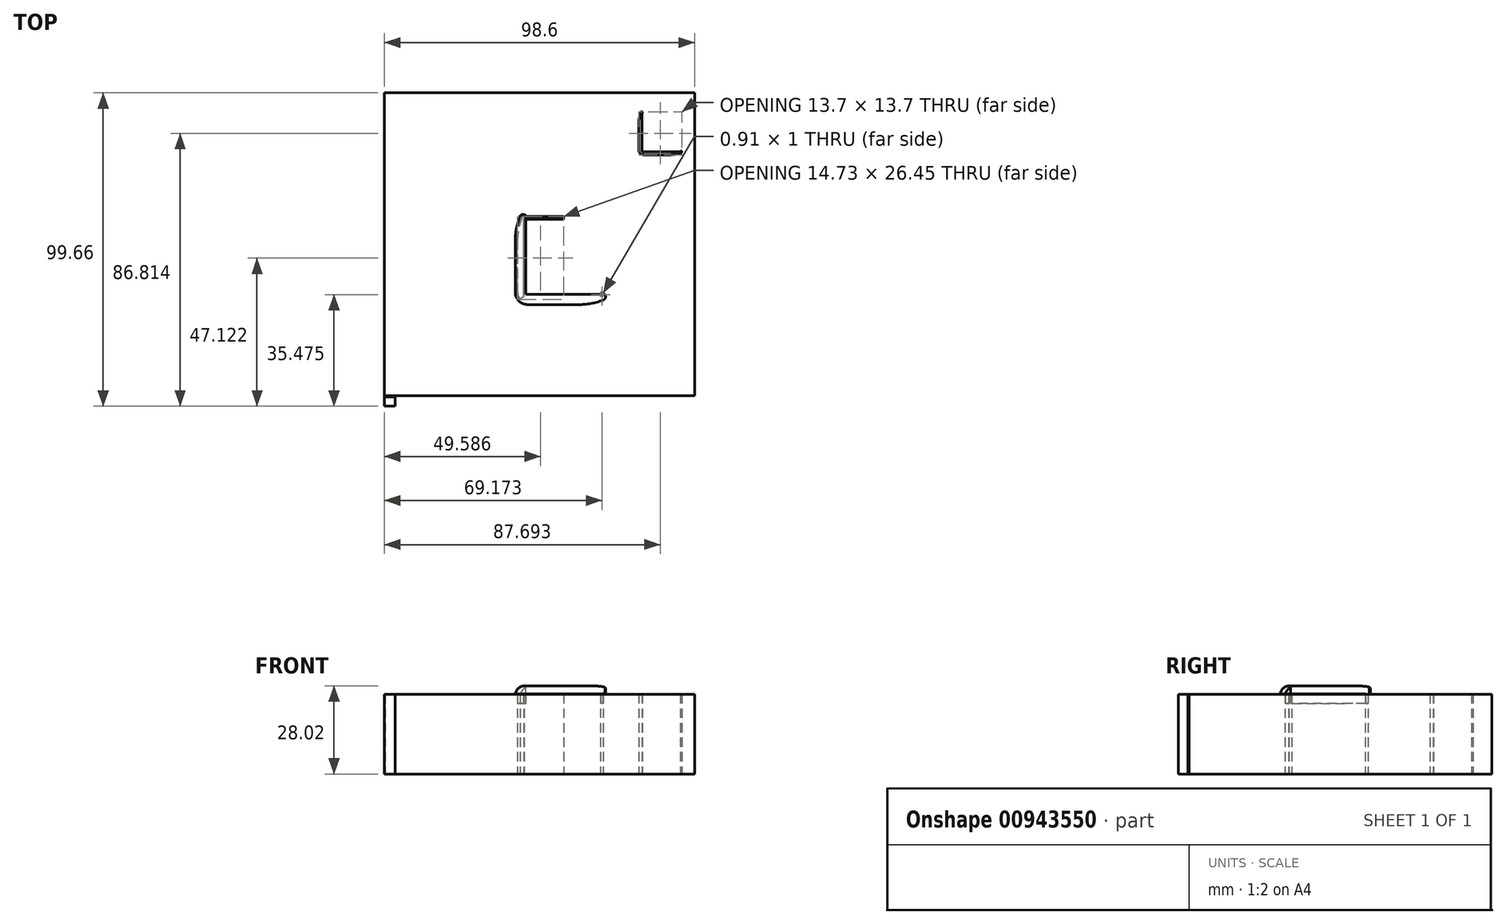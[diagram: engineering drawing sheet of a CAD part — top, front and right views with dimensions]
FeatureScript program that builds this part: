
annotation { "Feature Type Name" : "Feature", "Feature Type Description" : "" }
export const myFeature = defineFeature(function(context is Context, id is Id, definition is map)
    precondition{}
    {
        {
            var Q0;
            Q0=qCreatedBy(makeId("Top.planeOp"),FACE);
            var sketch = newSketch(context, id + "F0", { "sketchPlane" : qUnion([Q0])});
            skLineSegment(sketch, "E0", {"start": v(-49.3, -64.38) * mm, "end": v(49.3, -64.38) * mm});
            skLineSegment(sketch, "E1", {"start": v(49.3, -64.38) * mm, "end": v(49.3, 64.38) * mm});
            skLineSegment(sketch, "E2", {"start": v(49.3, 64.38) * mm, "end": v(-49.3, 64.38) * mm});
            skLineSegment(sketch, "E3", {"start": v(-49.3, 64.38) * mm, "end": v(-49.3, -64.38) * mm});
            skLineSegment(sketch, "E4", {"start": v(-49.3, 60.15) * mm, "end": v(49.3, 60.15) * mm});
            skLineSegment(sketch, "E5", {"start": v(49.3, 60.15) * mm, "end": v(49.3, 59.97) * mm});
            skLineSegment(sketch, "E6", {"start": v(49.3, 59.97) * mm, "end": v(-49.3, 59.97) * mm});
            skLineSegment(sketch, "E7", {"start": v(-49.3, 59.97) * mm, "end": v(-49.3, 60.15) * mm});
            skLineSegment(sketch, "E8", {"start": v(15.26, 64.38) * mm, "end": v(15.43, 64.38) * mm});
            skLineSegment(sketch, "E9", {"start": v(15.43, 64.38) * mm, "end": v(15.43, 59.97) * mm});
            skLineSegment(sketch, "E10", {"start": v(15.43, 59.97) * mm, "end": v(15.26, 59.97) * mm});
            skLineSegment(sketch, "E11", {"start": v(15.26, 59.97) * mm, "end": v(15.26, 64.38) * mm});
            skLineSegment(sketch, "E12", {"start": v(-49.12, -36.34) * mm, "end": v(49.3, -36.34) * mm});
            skLineSegment(sketch, "E13", {"start": v(49.3, -36.34) * mm, "end": v(49.3, -36.69) * mm});
            skLineSegment(sketch, "E14", {"start": v(49.3, -36.69) * mm, "end": v(-49.12, -36.69) * mm});
            skLineSegment(sketch, "E15", {"start": v(-49.12, -36.69) * mm, "end": v(-49.12, -36.34) * mm});
            skLineSegment(sketch, "E16", {"start": v(-6.44, -36.51) * mm, "end": v(-6.09, -36.51) * mm});
            skLineSegment(sketch, "E17", {"start": v(-6.09, -36.51) * mm, "end": v(-6.09, -64.2) * mm});
            skLineSegment(sketch, "E18", {"start": v(-6.09, -64.2) * mm, "end": v(-6.44, -64.2) * mm});
            skLineSegment(sketch, "E19", {"start": v(-6.44, -64.2) * mm, "end": v(-6.44, -36.51) * mm});
            skLineSegment(sketch, "E20", {"start": v(-6.44, -45.33) * mm, "end": v(49.12, -45.33) * mm});
            skLineSegment(sketch, "E21", {"start": v(49.12, -45.33) * mm, "end": v(49.12, -45.68) * mm});
            skLineSegment(sketch, "E22", {"start": v(49.12, -45.68) * mm, "end": v(-6.44, -45.68) * mm});
            skLineSegment(sketch, "E23", {"start": v(-6.44, -45.68) * mm, "end": v(-6.44, -45.33) * mm});
            skLineSegment(sketch, "E24", {"start": v(-6.44, -49.04) * mm, "end": v(49.12, -49.04) * mm});
            skLineSegment(sketch, "E25", {"start": v(49.12, -49.04) * mm, "end": v(49.12, -49.39) * mm});
            skLineSegment(sketch, "E26", {"start": v(49.12, -49.39) * mm, "end": v(-6.44, -49.39) * mm});
            skLineSegment(sketch, "E27", {"start": v(-6.44, -49.39) * mm, "end": v(-6.44, -49.04) * mm});
            skLineSegment(sketch, "E28", {"start": v(-6.09, -52.92) * mm, "end": v(49.3, -52.92) * mm});
            skLineSegment(sketch, "E29", {"start": v(49.3, -52.92) * mm, "end": v(49.3, -53.1) * mm});
            skLineSegment(sketch, "E30", {"start": v(49.3, -53.1) * mm, "end": v(-6.09, -53.1) * mm});
            skLineSegment(sketch, "E31", {"start": v(-6.09, -53.1) * mm, "end": v(-6.09, -52.92) * mm});
            skLineSegment(sketch, "E32", {"start": v(-6.09, -56.62) * mm, "end": v(49.3, -56.62) * mm});
            skLineSegment(sketch, "E33", {"start": v(49.3, -56.62) * mm, "end": v(49.3, -56.8) * mm});
            skLineSegment(sketch, "E34", {"start": v(49.3, -56.8) * mm, "end": v(-6.09, -56.8) * mm});
            skLineSegment(sketch, "E35", {"start": v(-6.09, -56.8) * mm, "end": v(-6.09, -56.62) * mm});
            skLineSegment(sketch, "E36", {"start": v(-6.09, -60.32) * mm, "end": v(49.3, -60.32) * mm});
            skLineSegment(sketch, "E37", {"start": v(49.3, -60.32) * mm, "end": v(49.3, -60.5) * mm});
            skLineSegment(sketch, "E38", {"start": v(49.3, -60.5) * mm, "end": v(-6.09, -60.5) * mm});
            skLineSegment(sketch, "E39", {"start": v(-6.09, -60.5) * mm, "end": v(-6.09, -60.32) * mm});
            skLineSegment(sketch, "E40", {"start": v(21.25, -49.04) * mm, "end": v(21.6, -49.04) * mm});
            skLineSegment(sketch, "E41", {"start": v(21.6, -49.04) * mm, "end": v(21.6, -64.2) * mm});
            skLineSegment(sketch, "E42", {"start": v(21.6, -64.2) * mm, "end": v(21.25, -64.2) * mm});
            skLineSegment(sketch, "E43", {"start": v(21.25, -64.2) * mm, "end": v(21.25, -49.04) * mm});
            skLineSegment(sketch, "E44", {"start": v(-49.3, -47.8) * mm, "end": v(-6.09, -47.8) * mm});
            skLineSegment(sketch, "E45", {"start": v(-6.09, -47.8) * mm, "end": v(-6.09, -48.15) * mm});
            skLineSegment(sketch, "E46", {"start": v(-6.09, -48.15) * mm, "end": v(-49.3, -48.15) * mm});
            skLineSegment(sketch, "E47", {"start": v(-49.3, -48.15) * mm, "end": v(-49.3, -47.8) * mm});
            skLineSegment(sketch, "E48", {"start": v(-49.3, -53.8) * mm, "end": v(-6.09, -53.8) * mm});
            skLineSegment(sketch, "E49", {"start": v(-6.09, -53.8) * mm, "end": v(-6.09, -50.98) * mm});
            skLineSegment(sketch, "E50", {"start": v(-6.09, -50.98) * mm, "end": v(-49.3, -50.98) * mm});
            skLineSegment(sketch, "E51", {"start": v(-49.3, -50.98) * mm, "end": v(-49.3, -53.8) * mm});
            skLineSegment(sketch, "E52", {"start": v(-49.3, -59.09) * mm, "end": v(-6.09, -59.09) * mm});
            skLineSegment(sketch, "E53", {"start": v(-6.09, -59.09) * mm, "end": v(-6.09, -56.27) * mm});
            skLineSegment(sketch, "E54", {"start": v(-6.09, -56.27) * mm, "end": v(-49.3, -56.27) * mm});
            skLineSegment(sketch, "E55", {"start": v(-49.3, -56.27) * mm, "end": v(-49.3, -59.09) * mm});
            skLineSegment(sketch, "E56", {"start": v(-49.3, -64.38) * mm, "end": v(-6.09, -64.38) * mm});
            skLineSegment(sketch, "E57", {"start": v(-6.09, -64.38) * mm, "end": v(-6.09, -61.56) * mm});
            skLineSegment(sketch, "E58", {"start": v(-6.09, -61.56) * mm, "end": v(-49.3, -61.56) * mm});
            skLineSegment(sketch, "E59", {"start": v(-49.3, -61.56) * mm, "end": v(-49.3, -64.38) * mm});
            skLineSegment(sketch, "E60", {"start": v(-49.3, -48.15) * mm, "end": v(-6.09, -48.15) * mm});
            skLineSegment(sketch, "E61", {"start": v(-6.09, -48.15) * mm, "end": v(-6.09, -45.33) * mm});
            skLineSegment(sketch, "E62", {"start": v(-6.09, -45.33) * mm, "end": v(-49.3, -45.33) * mm});
            skLineSegment(sketch, "E63", {"start": v(-49.3, -45.33) * mm, "end": v(-49.3, -48.15) * mm});
            skLineSegment(sketch, "E64", {"start": v(-49.3, -42.5) * mm, "end": v(-6.09, -42.5) * mm});
            skLineSegment(sketch, "E65", {"start": v(-6.09, -42.5) * mm, "end": v(-6.09, -39.69) * mm});
            skLineSegment(sketch, "E66", {"start": v(-6.09, -39.69) * mm, "end": v(-49.3, -39.69) * mm});
            skLineSegment(sketch, "E67", {"start": v(-49.3, -39.69) * mm, "end": v(-49.3, -42.5) * mm});
            skArc(sketch, "E68", {"start": v(-46.48, -62.8) * mm, "mid": v(-46.5, -62.62) * mm, "end": v(-46.54, -62.46) * mm});
            skArc(sketch, "E69", {"start": v(-46.54, -62.46) * mm, "mid": v(-46.63, -62.3) * mm, "end": v(-46.74, -62.17) * mm});
            skArc(sketch, "E70", {"start": v(-46.74, -62.17) * mm, "mid": v(-46.87, -62.06) * mm, "end": v(-47.02, -61.98) * mm});
            skArc(sketch, "E71", {"start": v(-47.02, -61.98) * mm, "mid": v(-47.19, -61.93) * mm, "end": v(-47.36, -61.91) * mm});
            skArc(sketch, "E72", {"start": v(-47.36, -61.91) * mm, "mid": v(-47.53, -61.93) * mm, "end": v(-47.7, -61.98) * mm});
            skArc(sketch, "E73", {"start": v(-47.7, -61.98) * mm, "mid": v(-47.85, -62.06) * mm, "end": v(-47.98, -62.17) * mm});
            skArc(sketch, "E74", {"start": v(-47.98, -62.17) * mm, "mid": v(-48.1, -62.3) * mm, "end": v(-48.17, -62.46) * mm});
            skArc(sketch, "E75", {"start": v(-48.17, -62.46) * mm, "mid": v(-48.22, -62.62) * mm, "end": v(-48.24, -62.8) * mm});
            skArc(sketch, "E76", {"start": v(-48.24, -62.8) * mm, "mid": v(-48.22, -62.97) * mm, "end": v(-48.17, -63.13) * mm});
            skArc(sketch, "E77", {"start": v(-48.17, -63.13) * mm, "mid": v(-48.1, -63.28) * mm, "end": v(-47.98, -63.42) * mm});
            skArc(sketch, "E78", {"start": v(-47.98, -63.42) * mm, "mid": v(-47.85, -63.53) * mm, "end": v(-47.7, -63.6) * mm});
            skArc(sketch, "E79", {"start": v(-47.7, -63.6) * mm, "mid": v(-47.53, -63.66) * mm, "end": v(-47.36, -63.68) * mm});
            skArc(sketch, "E80", {"start": v(-47.36, -63.68) * mm, "mid": v(-47.19, -63.66) * mm, "end": v(-47.02, -63.6) * mm});
            skArc(sketch, "E81", {"start": v(-47.02, -63.6) * mm, "mid": v(-46.87, -63.53) * mm, "end": v(-46.74, -63.42) * mm});
            skArc(sketch, "E82", {"start": v(-46.74, -63.42) * mm, "mid": v(-46.63, -63.28) * mm, "end": v(-46.54, -63.13) * mm});
            skArc(sketch, "E83", {"start": v(-46.54, -63.13) * mm, "mid": v(-46.5, -62.97) * mm, "end": v(-46.48, -62.8) * mm});
            skArc(sketch, "E84", {"start": v(-38.01, -62.8) * mm, "mid": v(-38.03, -62.62) * mm, "end": v(-38.08, -62.46) * mm});
            skArc(sketch, "E85", {"start": v(-38.08, -62.46) * mm, "mid": v(-38.16, -62.3) * mm, "end": v(-38.27, -62.17) * mm});
            skArc(sketch, "E86", {"start": v(-38.27, -62.17) * mm, "mid": v(-38.4, -62.06) * mm, "end": v(-38.56, -61.98) * mm});
            skArc(sketch, "E87", {"start": v(-38.56, -61.98) * mm, "mid": v(-38.72, -61.93) * mm, "end": v(-38.9, -61.91) * mm});
            skArc(sketch, "E88", {"start": v(-38.9, -61.91) * mm, "mid": v(-39.07, -61.93) * mm, "end": v(-39.23, -61.98) * mm});
            skArc(sketch, "E89", {"start": v(-39.23, -61.98) * mm, "mid": v(-39.38, -62.06) * mm, "end": v(-39.52, -62.17) * mm});
            skArc(sketch, "E90", {"start": v(-39.52, -62.17) * mm, "mid": v(-39.63, -62.3) * mm, "end": v(-39.7, -62.46) * mm});
            skArc(sketch, "E91", {"start": v(-39.7, -62.46) * mm, "mid": v(-39.76, -62.62) * mm, "end": v(-39.78, -62.8) * mm});
            skArc(sketch, "E92", {"start": v(-39.78, -62.8) * mm, "mid": v(-39.76, -62.97) * mm, "end": v(-39.7, -63.13) * mm});
            skArc(sketch, "E93", {"start": v(-39.7, -63.13) * mm, "mid": v(-39.63, -63.28) * mm, "end": v(-39.52, -63.42) * mm});
            skArc(sketch, "E94", {"start": v(-39.52, -63.42) * mm, "mid": v(-39.38, -63.53) * mm, "end": v(-39.23, -63.6) * mm});
            skArc(sketch, "E95", {"start": v(-39.23, -63.6) * mm, "mid": v(-39.07, -63.66) * mm, "end": v(-38.9, -63.68) * mm});
            skArc(sketch, "E96", {"start": v(-38.9, -63.68) * mm, "mid": v(-38.72, -63.66) * mm, "end": v(-38.56, -63.6) * mm});
            skArc(sketch, "E97", {"start": v(-38.56, -63.6) * mm, "mid": v(-38.4, -63.53) * mm, "end": v(-38.27, -63.42) * mm});
            skArc(sketch, "E98", {"start": v(-38.27, -63.42) * mm, "mid": v(-38.16, -63.28) * mm, "end": v(-38.08, -63.13) * mm});
            skArc(sketch, "E99", {"start": v(-38.08, -63.13) * mm, "mid": v(-38.03, -62.97) * mm, "end": v(-38.01, -62.8) * mm});
            skArc(sketch, "E100", {"start": v(-23.55, -62.8) * mm, "mid": v(-23.56, -62.62) * mm, "end": v(-23.62, -62.46) * mm});
            skArc(sketch, "E101", {"start": v(-23.62, -62.46) * mm, "mid": v(-23.7, -62.3) * mm, "end": v(-23.8, -62.17) * mm});
            skArc(sketch, "E102", {"start": v(-23.8, -62.17) * mm, "mid": v(-23.94, -62.06) * mm, "end": v(-24.1, -61.98) * mm});
            skArc(sketch, "E103", {"start": v(-24.1, -61.98) * mm, "mid": v(-24.26, -61.93) * mm, "end": v(-24.43, -61.91) * mm});
            skArc(sketch, "E104", {"start": v(-24.43, -61.91) * mm, "mid": v(-24.6, -61.93) * mm, "end": v(-24.77, -61.98) * mm});
            skArc(sketch, "E105", {"start": v(-24.77, -61.98) * mm, "mid": v(-24.92, -62.06) * mm, "end": v(-25.05, -62.17) * mm});
            skArc(sketch, "E106", {"start": v(-25.05, -62.17) * mm, "mid": v(-25.16, -62.3) * mm, "end": v(-25.24, -62.46) * mm});
            skArc(sketch, "E107", {"start": v(-25.24, -62.46) * mm, "mid": v(-25.3, -62.62) * mm, "end": v(-25.31, -62.8) * mm});
            skArc(sketch, "E108", {"start": v(-25.31, -62.8) * mm, "mid": v(-25.3, -62.97) * mm, "end": v(-25.24, -63.13) * mm});
            skArc(sketch, "E109", {"start": v(-25.24, -63.13) * mm, "mid": v(-25.16, -63.28) * mm, "end": v(-25.05, -63.42) * mm});
            skArc(sketch, "E110", {"start": v(-25.05, -63.42) * mm, "mid": v(-24.92, -63.53) * mm, "end": v(-24.77, -63.6) * mm});
            skArc(sketch, "E111", {"start": v(-24.77, -63.6) * mm, "mid": v(-24.6, -63.66) * mm, "end": v(-24.43, -63.68) * mm});
            skArc(sketch, "E112", {"start": v(-24.43, -63.68) * mm, "mid": v(-24.26, -63.66) * mm, "end": v(-24.1, -63.6) * mm});
            skArc(sketch, "E113", {"start": v(-24.1, -63.6) * mm, "mid": v(-23.94, -63.53) * mm, "end": v(-23.8, -63.42) * mm});
            skArc(sketch, "E114", {"start": v(-23.8, -63.42) * mm, "mid": v(-23.7, -63.28) * mm, "end": v(-23.62, -63.13) * mm});
            skArc(sketch, "E115", {"start": v(-23.62, -63.13) * mm, "mid": v(-23.56, -62.97) * mm, "end": v(-23.55, -62.8) * mm});
            skLineSegment(sketch, "E116", {"start": v(-4.68, -39.46) * mm, "end": v(-4.68, -39.2) * mm});
            skLineSegment(sketch, "E117", {"start": v(-4.68, -39.2) * mm, "end": v(-2.48, -39.2) * mm});
            skLineSegment(sketch, "E118", {"start": v(-2.48, -39.2) * mm, "end": v(-2.48, -38.95) * mm});
            skLineSegment(sketch, "E119", {"start": v(-2.48, -38.95) * mm, "end": v(-4.68, -38.95) * mm});
            skLineSegment(sketch, "E120", {"start": v(-4.68, -38.95) * mm, "end": v(-4.68, -37.29) * mm});
            skLineSegment(sketch, "E121", {"start": v(-4.68, -37.29) * mm, "end": v(-1.9, -37.29) * mm});
            skArc(sketch, "E122", {"start": v(-1.9, -37.3) * mm, "mid": v(-1.01, -37.67) * mm, "end": v(-0.64, -38.57) * mm});
            skArc(sketch, "E123", {"start": v(-0.64, -38.57) * mm, "mid": v(-1.01, -39.46) * mm, "end": v(-1.9, -39.84) * mm});
            skLineSegment(sketch, "E124", {"start": v(-1.9, -39.84) * mm, "end": v(-2.48, -39.84) * mm});
            skLineSegment(sketch, "E125", {"start": v(-2.48, -39.84) * mm, "end": v(-2.48, -39.97) * mm});
            skLineSegment(sketch, "E126", {"start": v(-2.48, -39.97) * mm, "end": v(-4.68, -39.97) * mm});
            skLineSegment(sketch, "E127", {"start": v(-4.68, -39.97) * mm, "end": v(-4.68, -39.72) * mm});
            skLineSegment(sketch, "E128", {"start": v(-4.68, -39.72) * mm, "end": v(-2.48, -39.72) * mm});
            skLineSegment(sketch, "E129", {"start": v(-2.48, -39.72) * mm, "end": v(-2.48, -39.46) * mm});
            skLineSegment(sketch, "E130", {"start": v(-2.48, -39.46) * mm, "end": v(-4.68, -39.46) * mm});
            skLineSegment(sketch, "E131", {"start": v(-2.48, -40.23) * mm, "end": v(-4.68, -40.23) * mm});
            skLineSegment(sketch, "E132", {"start": v(-2.48, -40.48) * mm, "end": v(-4.68, -40.48) * mm});
            skLineSegment(sketch, "E133", {"start": v(-4.68, -40.48) * mm, "end": v(-4.68, -40.23) * mm});
            skLineSegment(sketch, "E134", {"start": v(-2.48, -40.23) * mm, "end": v(-2.48, -40.48) * mm});
            skLineSegment(sketch, "E135", {"start": v(2.09, -38.5) * mm, "end": v(3.79, -39.27) * mm});
            skLineSegment(sketch, "E136", {"start": v(2.53, -39.59) * mm, "end": v(1.84, -39.59) * mm});
            skLineSegment(sketch, "E137", {"start": v(0.7, -37.29) * mm, "end": v(4.11, -37.29) * mm});
            skLineSegment(sketch, "E138", {"start": v(0.7, -37.29) * mm, "end": v(2.68, -38.18) * mm});
            skLineSegment(sketch, "E139", {"start": v(-0.28, -37.73) * mm, "end": v(3.13, -39.27) * mm});
            skLineSegment(sketch, "E140", {"start": v(2.09, -38.5) * mm, "end": v(2.74, -38.5) * mm});
            skLineSegment(sketch, "E141", {"start": v(4.11, -40.48) * mm, "end": v(-0.28, -40.48) * mm});
            skLineSegment(sketch, "E142", {"start": v(-0.28, -38.32) * mm, "end": v(-0.28, -40.48) * mm});
            skLineSegment(sketch, "E143", {"start": v(1.84, -39.27) * mm, "end": v(1.84, -39.59) * mm});
            skLineSegment(sketch, "E144", {"start": v(-0.28, -37.44) * mm, "end": v(1.84, -38.39) * mm});
            skLineSegment(sketch, "E145", {"start": v(0.05, -37.29) * mm, "end": v(2.03, -38.18) * mm});
            skLineSegment(sketch, "E146", {"start": v(-0.28, -37.73) * mm, "end": v(-0.28, -38.03) * mm});
            skLineSegment(sketch, "E147", {"start": v(-0.28, -37.29) * mm, "end": v(0.05, -37.29) * mm});
            skLineSegment(sketch, "E148", {"start": v(-0.28, -37.29) * mm, "end": v(-0.28, -37.44) * mm});
            skLineSegment(sketch, "E149", {"start": v(1.84, -38.18) * mm, "end": v(1.84, -38.39) * mm});
            skLineSegment(sketch, "E150", {"start": v(1.84, -38.18) * mm, "end": v(2.03, -38.18) * mm});
            skLineSegment(sketch, "E151", {"start": v(3.4, -38.5) * mm, "end": v(4.11, -38.83) * mm});
            skLineSegment(sketch, "E152", {"start": v(2.74, -38.5) * mm, "end": v(4.11, -39.12) * mm});
            skLineSegment(sketch, "E153", {"start": v(4.11, -38.5) * mm, "end": v(4.11, -38.83) * mm});
            skLineSegment(sketch, "E154", {"start": v(3.84, -39.59) * mm, "end": v(4.11, -39.71) * mm});
            skLineSegment(sketch, "E155", {"start": v(2.53, -39.59) * mm, "end": v(4.11, -40.3) * mm});
            skLineSegment(sketch, "E156", {"start": v(3.19, -39.59) * mm, "end": v(4.11, -40) * mm});
            skLineSegment(sketch, "E157", {"start": v(4.11, -39.27) * mm, "end": v(3.79, -39.27) * mm});
            skLineSegment(sketch, "E158", {"start": v(3.13, -39.27) * mm, "end": v(2.48, -39.27) * mm});
            skLineSegment(sketch, "E159", {"start": v(3.84, -39.59) * mm, "end": v(3.19, -39.59) * mm});
            skLineSegment(sketch, "E160", {"start": v(4.11, -40.3) * mm, "end": v(4.11, -40.48) * mm});
            skLineSegment(sketch, "E161", {"start": v(4.11, -39.12) * mm, "end": v(4.11, -39.27) * mm});
            skLineSegment(sketch, "E162", {"start": v(4.11, -39.71) * mm, "end": v(4.11, -40) * mm});
            skLineSegment(sketch, "E163", {"start": v(2.68, -38.18) * mm, "end": v(4.11, -38.18) * mm});
            skLineSegment(sketch, "E164", {"start": v(3.4, -38.5) * mm, "end": v(4.11, -38.5) * mm});
            skLineSegment(sketch, "E165", {"start": v(4.11, -37.29) * mm, "end": v(4.11, -38.18) * mm});
            skLineSegment(sketch, "E166", {"start": v(-0.28, -38.32) * mm, "end": v(-0.28, -38.03) * mm});
            skLineSegment(sketch, "E167", {"start": v(1.84, -39.27) * mm, "end": v(2.48, -39.27) * mm});
            skLineSegment(sketch, "E168", {"start": v(-49.12, -36.34) * mm, "end": v(-45.95, -36.34) * mm});
            skLineSegment(sketch, "E169", {"start": v(-45.95, -36.34) * mm, "end": v(-45.95, -47.8) * mm});
            skLineSegment(sketch, "E170", {"start": v(-2.58, -40.48) * mm, "end": v(-2.48, -40.43) * mm});
            skLineSegment(sketch, "E171", {"start": v(1.97, -37.86) * mm, "end": v(2.95, -37.29) * mm});
            skLineSegment(sketch, "E172", {"start": v(-1.32, -39.76) * mm, "end": v(-0.63, -39.36) * mm});
            skLineSegment(sketch, "E173", {"start": v(1.4, -38.2) * mm, "end": v(1.68, -38.03) * mm});
            skLineSegment(sketch, "E174", {"start": v(-0.28, -39.16) * mm, "end": v(1.1, -38.36) * mm});
            skLineSegment(sketch, "E175", {"start": v(-3.21, -40.48) * mm, "end": v(-2.77, -40.23) * mm});
            skLineSegment(sketch, "E176", {"start": v(1.6, -37.7) * mm, "end": v(2.32, -37.29) * mm});
            skLineSegment(sketch, "E177", {"start": v(-2.1, -39.84) * mm, "end": v(-0.31, -38.8) * mm});
            skLineSegment(sketch, "E178", {"start": v(1.04, -38.03) * mm, "end": v(1.32, -37.86) * mm});
            skLineSegment(sketch, "E179", {"start": v(-0.28, -38.8) * mm, "end": v(0.75, -38.2) * mm});
            skLineSegment(sketch, "E180", {"start": v(-3.85, -40.48) * mm, "end": v(-3.4, -40.23) * mm});
            skLineSegment(sketch, "E181", {"start": v(1.25, -37.54) * mm, "end": v(1.68, -37.29) * mm});
            skLineSegment(sketch, "E182", {"start": v(-2.96, -39.97) * mm, "end": v(-2.52, -39.72) * mm});
            skLineSegment(sketch, "E183", {"start": v(0.68, -37.87) * mm, "end": v(0.97, -37.7) * mm});
            skLineSegment(sketch, "E184", {"start": v(-2.48, -39.7) * mm, "end": v(-0.3, -38.43) * mm});
            skLineSegment(sketch, "E185", {"start": v(-0.28, -38.42) * mm, "end": v(0.4, -38.03) * mm});
            skLineSegment(sketch, "E186", {"start": v(-4.48, -40.48) * mm, "end": v(-4.04, -40.23) * mm});
            skLineSegment(sketch, "E187", {"start": v(0.9, -37.38) * mm, "end": v(1.05, -37.29) * mm});
            skLineSegment(sketch, "E188", {"start": v(-3.6, -39.97) * mm, "end": v(-3.15, -39.72) * mm});
            skLineSegment(sketch, "E189", {"start": v(0.32, -37.7) * mm, "end": v(0.6, -37.54) * mm});
            skLineSegment(sketch, "E190", {"start": v(-2.71, -39.46) * mm, "end": v(-0.39, -38.12) * mm});
            skLineSegment(sketch, "E191", {"start": v(-0.28, -38.06) * mm, "end": v(0.04, -37.87) * mm});
            skLineSegment(sketch, "E192", {"start": v(-4.68, -40.23) * mm, "end": v(-4.67, -40.23) * mm});
            skLineSegment(sketch, "E193", {"start": v(-0.03, -37.55) * mm, "end": v(0.25, -37.38) * mm});
            skLineSegment(sketch, "E194", {"start": v(-4.23, -39.97) * mm, "end": v(-3.79, -39.72) * mm});
            skLineSegment(sketch, "E195", {"start": v(-2.48, -38.96) * mm, "end": v(-0.56, -37.85) * mm});
            skLineSegment(sketch, "E196", {"start": v(-3.35, -39.46) * mm, "end": v(-2.9, -39.2) * mm});
            skLineSegment(sketch, "E197", {"start": v(-4.68, -39.86) * mm, "end": v(-4.42, -39.72) * mm});
            skLineSegment(sketch, "E198", {"start": v(-0.28, -37.32) * mm, "end": v(-0.22, -37.29) * mm});
            skLineSegment(sketch, "E199", {"start": v(-3.98, -39.46) * mm, "end": v(-3.54, -39.2) * mm});
            skLineSegment(sketch, "E200", {"start": v(-3.1, -38.95) * mm, "end": v(-0.8, -37.63) * mm});
            skLineSegment(sketch, "E201", {"start": v(-4.62, -39.46) * mm, "end": v(-4.18, -39.2) * mm});
            skLineSegment(sketch, "E202", {"start": v(-3.73, -38.95) * mm, "end": v(-1.13, -37.45) * mm});
            skLineSegment(sketch, "E203", {"start": v(-4.37, -38.95) * mm, "end": v(-1.55, -37.32) * mm});
            skLineSegment(sketch, "E204", {"start": v(-4.68, -38.76) * mm, "end": v(-2.13, -37.29) * mm});
            skLineSegment(sketch, "E205", {"start": v(-4.68, -38.4) * mm, "end": v(-2.76, -37.29) * mm});
            skLineSegment(sketch, "E206", {"start": v(-4.68, -38.03) * mm, "end": v(-3.4, -37.29) * mm});
            skLineSegment(sketch, "E207", {"start": v(-4.68, -37.66) * mm, "end": v(-4.03, -37.29) * mm});
            skLineSegment(sketch, "E208", {"start": v(-4.68, -37.3) * mm, "end": v(-4.67, -37.29) * mm});
            skLineSegment(sketch, "E209", {"start": v(-0.28, -39.52) * mm, "end": v(1.46, -38.52) * mm});
            skLineSegment(sketch, "E210", {"start": v(2.32, -38.02) * mm, "end": v(3.59, -37.29) * mm});
            skLineSegment(sketch, "E211", {"start": v(1.75, -38.35) * mm, "end": v(1.84, -38.3) * mm});
            skLineSegment(sketch, "E212", {"start": v(-0.28, -39.9) * mm, "end": v(1.82, -38.68) * mm});
            skLineSegment(sketch, "E213", {"start": v(2.68, -38.18) * mm, "end": v(4.11, -37.35) * mm});
            skLineSegment(sketch, "E214", {"start": v(2.1, -38.51) * mm, "end": v(2.12, -38.5) * mm});
            skLineSegment(sketch, "E215", {"start": v(-0.28, -40.26) * mm, "end": v(2.18, -38.84) * mm});
            skLineSegment(sketch, "E216", {"start": v(3.3, -38.18) * mm, "end": v(4.11, -37.72) * mm});
            skLineSegment(sketch, "E217", {"start": v(2.46, -38.67) * mm, "end": v(2.75, -38.5) * mm});
            skLineSegment(sketch, "E218", {"start": v(-0.04, -40.48) * mm, "end": v(1.84, -39.4) * mm});
            skLineSegment(sketch, "E219", {"start": v(3.94, -38.18) * mm, "end": v(4.11, -38.09) * mm});
            skLineSegment(sketch, "E220", {"start": v(2.06, -39.27) * mm, "end": v(2.53, -39) * mm});
            skLineSegment(sketch, "E221", {"start": v(2.82, -38.83) * mm, "end": v(3.1, -38.67) * mm});
            skLineSegment(sketch, "E222", {"start": v(0.6, -40.48) * mm, "end": v(2.15, -39.59) * mm});
            skLineSegment(sketch, "E223", {"start": v(3.75, -38.66) * mm, "end": v(4.03, -38.5) * mm});
            skLineSegment(sketch, "E224", {"start": v(2.7, -39.27) * mm, "end": v(2.89, -39.16) * mm});
            skLineSegment(sketch, "E225", {"start": v(3.18, -39) * mm, "end": v(3.46, -38.83) * mm});
            skLineSegment(sketch, "E226", {"start": v(1.23, -40.48) * mm, "end": v(2.67, -39.65) * mm});
            skLineSegment(sketch, "E227", {"start": v(4.1, -38.82) * mm, "end": v(4.11, -38.82) * mm});
            skLineSegment(sketch, "E228", {"start": v(3.53, -39.15) * mm, "end": v(3.82, -38.99) * mm});
            skLineSegment(sketch, "E229", {"start": v(1.87, -40.48) * mm, "end": v(3.03, -39.81) * mm});
            skLineSegment(sketch, "E230", {"start": v(3.97, -39.27) * mm, "end": v(4.11, -39.19) * mm});
            skLineSegment(sketch, "E231", {"start": v(3.32, -39.65) * mm, "end": v(3.42, -39.59) * mm});
            skLineSegment(sketch, "E232", {"start": v(2.5, -40.48) * mm, "end": v(3.39, -39.97) * mm});
            skLineSegment(sketch, "E233", {"start": v(3.67, -39.8) * mm, "end": v(3.96, -39.64) * mm});
            skLineSegment(sketch, "E234", {"start": v(3.14, -40.48) * mm, "end": v(3.74, -40.13) * mm});
            skLineSegment(sketch, "E235", {"start": v(4.03, -39.97) * mm, "end": v(4.11, -39.92) * mm});
            skLineSegment(sketch, "E236", {"start": v(3.77, -40.48) * mm, "end": v(4.1, -40.3) * mm});
            skLineSegment(sketch, "E237", {"start": v(6.9, 7.22) * mm, "end": v(-11.38, -11.05) * mm});
            skLineSegment(sketch, "E238", {"start": v(44.8, 41.29) * mm, "end": v(32.79, 41.29) * mm});
            skArc(sketch, "E239", {"start": v(32.79, 41.29) * mm, "mid": v(32.7, 41.3) * mm, "end": v(32.62, 41.36) * mm});
            skArc(sketch, "E240", {"start": v(32.62, 41.36) * mm, "mid": v(32.57, 41.43) * mm, "end": v(32.56, 41.52) * mm});
            skLineSegment(sketch, "E241", {"start": v(32.56, 41.52) * mm, "end": v(32.56, 53.52) * mm});
            skArc(sketch, "E242", {"start": v(32.56, 53.52) * mm, "mid": v(32.75, 53.77) * mm, "end": v(32.52, 53.98) * mm});
            skLineSegment(sketch, "E243", {"start": v(32.52, 53.98) * mm, "end": v(32.46, 53.98) * mm});
            skArc(sketch, "E244", {"start": v(32.46, 53.98) * mm, "mid": v(32.33, 53.94) * mm, "end": v(32.24, 53.83) * mm});
            skArc(sketch, "E245", {"start": v(32.24, 53.83) * mm, "mid": v(31.72, 52.07) * mm, "end": v(31.54, 50.24) * mm});
            skLineSegment(sketch, "E246", {"start": v(31.54, 50.24) * mm, "end": v(31.54, 41.9) * mm});
            skArc(sketch, "E247", {"start": v(31.54, 41.9) * mm, "mid": v(31.67, 41.28) * mm, "end": v(32.02, 40.75) * mm});
            skArc(sketch, "E248", {"start": v(32.02, 40.75) * mm, "mid": v(32.55, 40.4) * mm, "end": v(33.17, 40.27) * mm});
            skLineSegment(sketch, "E249", {"start": v(33.17, 40.27) * mm, "end": v(41.51, 40.27) * mm});
            skArc(sketch, "E250", {"start": v(41.51, 40.27) * mm, "mid": v(43.34, 40.45) * mm, "end": v(45.1, 40.98) * mm});
            skArc(sketch, "E251", {"start": v(45.1, 40.98) * mm, "mid": v(45.2, 41.06) * mm, "end": v(45.24, 41.19) * mm});
            skLineSegment(sketch, "E252", {"start": v(45.24, 41.19) * mm, "end": v(45.24, 41.25) * mm});
            skArc(sketch, "E253", {"start": v(45.24, 41.25) * mm, "mid": v(45.03, 41.48) * mm, "end": v(44.8, 41.29) * mm});
            skLineSegment(sketch, "E254", {"start": v(19.42, -4.72) * mm, "end": v(-4.6, -4.72) * mm});
            skArc(sketch, "E255", {"start": v(-4.6, -4.72) * mm, "mid": v(-4.77, -4.68) * mm, "end": v(-4.91, -4.58) * mm});
            skArc(sketch, "E256", {"start": v(-4.91, -4.58) * mm, "mid": v(-5.01, -4.43) * mm, "end": v(-5.05, -4.26) * mm});
            skLineSegment(sketch, "E257", {"start": v(-5.05, -4.26) * mm, "end": v(-5.05, 19.75) * mm});
            skArc(sketch, "E258", {"start": v(-5.05, 19.75) * mm, "mid": v(-4.67, 20.24) * mm, "end": v(-5.12, 20.66) * mm});
            skLineSegment(sketch, "E259", {"start": v(-5.12, 20.66) * mm, "end": v(-5.25, 20.66) * mm});
            skArc(sketch, "E260", {"start": v(-5.25, 20.66) * mm, "mid": v(-5.5, 20.58) * mm, "end": v(-5.67, 20.37) * mm});
            skArc(sketch, "E261", {"start": v(-5.67, 20.37) * mm, "mid": v(-6.73, 16.85) * mm, "end": v(-7.08, 13.2) * mm});
            skLineSegment(sketch, "E262", {"start": v(-7.08, 13.2) * mm, "end": v(-7.08, -3.49) * mm});
            skArc(sketch, "E263", {"start": v(-7.08, -3.49) * mm, "mid": v(-6.83, -4.74) * mm, "end": v(-6.13, -5.8) * mm});
            skArc(sketch, "E264", {"start": v(-6.13, -5.8) * mm, "mid": v(-5.07, -6.5) * mm, "end": v(-3.82, -6.75) * mm});
            skLineSegment(sketch, "E265", {"start": v(-3.82, -6.75) * mm, "end": v(12.86, -6.75) * mm});
            skArc(sketch, "E266", {"start": v(12.86, -6.75) * mm, "mid": v(16.52, -6.4) * mm, "end": v(20.04, -5.34) * mm});
            skArc(sketch, "E267", {"start": v(20.04, -5.34) * mm, "mid": v(20.25, -5.17) * mm, "end": v(20.33, -4.92) * mm});
            skLineSegment(sketch, "E268", {"start": v(20.33, -4.92) * mm, "end": v(20.33, -4.8) * mm});
            skArc(sketch, "E269", {"start": v(20.33, -4.8) * mm, "mid": v(19.9, -4.34) * mm, "end": v(19.42, -4.72) * mm});
            skSolve(sketch);
        }
        {
            var Q0;
            Q0=makeQuery(id+"F0.imprint","IMPRINT",FACE,{"disambiguationData":[TD([[makeQuery(id+"F0.imprint","IMPRINT",EDGE,{"derivedFrom":sQuery(id+"F0.wireOp",EDGE,"E254")}),1.0]])]});
            var Q1;
            {var subQ0=sQuery(id+"F0.wireOp",EDGE,"E256");Q1=makeQuery(id+"F0.imprint","IMPRINT",FACE,{"disambiguationData":[TD([[makeQuery(id+"F0.imprint","IMPRINT",EDGE,{"derivedFrom":subQ0}),1.0]])]});}
            extrude(context, id + "F1", {"entities" : qUnion([Q0, Q1]), "depth" : 25.4 * mm});
        }
        {
            var Q0;
            Q0=makeQuery(id+"F1.opExtrude","CAP_FACE",FACE,{"disambiguationData":[OSD([sQuery(id+"F0.wireOp",EDGE,"E254"),sQuery(id+"F0.wireOp",EDGE,"E255"),sQuery(id+"F0.wireOp",EDGE,"E256"),sQuery(id+"F0.wireOp",EDGE,"E257"),sQuery(id+"F0.wireOp",EDGE,"E258"),sQuery(id+"F0.wireOp",EDGE,"E259"),sQuery(id+"F0.wireOp",EDGE,"E260"),sQuery(id+"F0.wireOp",EDGE,"E261"),sQuery(id+"F0.wireOp",EDGE,"E262"),sQuery(id+"F0.wireOp",EDGE,"E263"),sQuery(id+"F0.wireOp",EDGE,"E264"),sQuery(id+"F0.wireOp",EDGE,"E265"),sQuery(id+"F0.wireOp",EDGE,"E266"),sQuery(id+"F0.wireOp",EDGE,"E267"),sQuery(id+"F0.wireOp",EDGE,"E268"),sQuery(id+"F0.wireOp",EDGE,"E269")])],"isStart":true});
            var sketch = newSketch(context, id + "F2", { "sketchPlane" : qUnion([Q0])});
            skLineSegment(sketch, "E270.bottom", {"start": v(19.42, 4.72) * mm, "end": v(20.33, 4.72) * mm});
            skLineSegment(sketch, "E270.top", {"start": v(19.42, 3.71) * mm, "end": v(20.33, 3.71) * mm});
            skLineSegment(sketch, "E270.left", {"start": v(19.42, 4.72) * mm, "end": v(19.42, 3.71) * mm});
            skLineSegment(sketch, "E270.right", {"start": v(20.33, 4.72) * mm, "end": v(20.33, 3.71) * mm});
            skSolve(sketch);
        }
        {
            var Q0;
            Q0=qSketchRegion(id+"F2",true);
            extrude(context, id + "F3", {"entities" : qUnion([Q0]), "operationType" : NewBodyOperationType.REMOVE, "endBound" : BoundingType.THROUGH_ALL, "oppositeDirection" : true, "depth" : 25.4 * mm});
        }
        {
            var Q0;
            Q0=makeQuery(id+"F1.opExtrude","CAP_FACE",FACE,{"disambiguationData":[OSD([sQuery(id+"F0.wireOp",EDGE,"E254"),sQuery(id+"F0.wireOp",EDGE,"E255"),sQuery(id+"F0.wireOp",EDGE,"E256"),sQuery(id+"F0.wireOp",EDGE,"E257"),sQuery(id+"F0.wireOp",EDGE,"E258"),sQuery(id+"F0.wireOp",EDGE,"E259"),sQuery(id+"F0.wireOp",EDGE,"E260"),sQuery(id+"F0.wireOp",EDGE,"E261"),sQuery(id+"F0.wireOp",EDGE,"E262"),sQuery(id+"F0.wireOp",EDGE,"E263"),sQuery(id+"F0.wireOp",EDGE,"E264"),sQuery(id+"F0.wireOp",EDGE,"E265"),sQuery(id+"F0.wireOp",EDGE,"E266"),sQuery(id+"F0.wireOp",EDGE,"E267"),sQuery(id+"F0.wireOp",EDGE,"E268"),sQuery(id+"F0.wireOp",EDGE,"E269")])],"isStart":true});
            var sketch = newSketch(context, id + "F4", { "sketchPlane" : qUnion([Q0])});
            skLineSegment(sketch, "E271.bottom", {"start": v(7.65, -20.65) * mm, "end": v(-5.05, -20.65) * mm});
            skLineSegment(sketch, "E271.top", {"start": v(7.65, -19.75) * mm, "end": v(-5.05, -19.75) * mm});
            skLineSegment(sketch, "E271.left", {"start": v(7.65, -20.65) * mm, "end": v(7.65, -19.75) * mm});
            skLineSegment(sketch, "E271.right", {"start": v(-5.05, -20.65) * mm, "end": v(-5.05, -19.75) * mm});
            skSolve(sketch);
        }
        {
            var Q0;
            Q0=qSketchRegion(id+"F4",true);
            extrude(context, id + "F5", {"entities" : qUnion([Q0]), "operationType" : NewBodyOperationType.REMOVE, "endBound" : BoundingType.THROUGH_ALL, "oppositeDirection" : true, "depth" : 25.4 * mm});
        }
        {
            var Q0;
            Q0=makeQuery(id+"F1.opExtrude","CAP_FACE",FACE,{"disambiguationData":[OSD([sQuery(id+"F0.wireOp",EDGE,"E254"),sQuery(id+"F0.wireOp",EDGE,"E255"),sQuery(id+"F0.wireOp",EDGE,"E256"),sQuery(id+"F0.wireOp",EDGE,"E257"),sQuery(id+"F0.wireOp",EDGE,"E258"),sQuery(id+"F0.wireOp",EDGE,"E259"),sQuery(id+"F0.wireOp",EDGE,"E260"),sQuery(id+"F0.wireOp",EDGE,"E261"),sQuery(id+"F0.wireOp",EDGE,"E262"),sQuery(id+"F0.wireOp",EDGE,"E263"),sQuery(id+"F0.wireOp",EDGE,"E264"),sQuery(id+"F0.wireOp",EDGE,"E265"),sQuery(id+"F0.wireOp",EDGE,"E266"),sQuery(id+"F0.wireOp",EDGE,"E267"),sQuery(id+"F0.wireOp",EDGE,"E268"),sQuery(id+"F0.wireOp",EDGE,"E269")])],"isStart":false});
            var sketch = newSketch(context, id + "F6", { "sketchPlane" : qUnion([Q0])});
            skLineSegment(sketch, "E272.0", {"start": v(-7.74, 13.2) * mm, "end": v(-7.74, -3.49) * mm});
            skArc(sketch, "E272.1", {"start": v(-6.29, 20.62) * mm, "mid": v(-7.37, 16.98) * mm, "end": v(-7.74, 13.2) * mm});
            skLineSegment(sketch, "E272.2", {"start": v(20.99, -4.92) * mm, "end": v(20.99, -4.8) * mm});
            skArc(sketch, "E272.3", {"start": v(20.3, -5.95) * mm, "mid": v(20.8, -5.54) * mm, "end": v(20.99, -4.92) * mm});
            skArc(sketch, "E272.4", {"start": v(12.86, -7.4) * mm, "mid": v(16.65, -7.04) * mm, "end": v(20.3, -5.95) * mm});
            skLineSegment(sketch, "E272.5", {"start": v(-3.82, -7.4) * mm, "end": v(12.86, -7.4) * mm});
            skArc(sketch, "E272.6", {"start": v(20.99, -4.8) * mm, "mid": v(20.92, -4.4) * mm, "end": v(20.7, -4.06) * mm});
            skLineSegment(sketch, "E272.7", {"start": v(20.7, -4.06) * mm, "end": v(-4.39, -4.06) * mm});
            skLineSegment(sketch, "E272.8", {"start": v(-4.39, -4.06) * mm, "end": v(-4.39, 21.04) * mm});
            skArc(sketch, "E272.9", {"start": v(-4.39, 21.04) * mm, "mid": v(-4.73, 21.25) * mm, "end": v(-5.12, 21.32) * mm});
            skLineSegment(sketch, "E272.10", {"start": v(-5.12, 21.32) * mm, "end": v(-5.25, 21.32) * mm});
            skArc(sketch, "E272.11", {"start": v(-5.25, 21.32) * mm, "mid": v(-5.87, 21.13) * mm, "end": v(-6.29, 20.62) * mm});
            skArc(sketch, "E273.0", {"start": v(-7.74, -3.49) * mm, "mid": v(-6.6, -6.26) * mm, "end": v(-3.82, -7.4) * mm});
            skSolve(sketch);
        }
        {
            var Q0;
            Q0=qSketchRegion(id+"F6",true);
            extrude(context, id + "F7", {"entities" : qUnion([Q0]), "oppositeDirection" : true, "offsetDistance" : 25.4 * mm, "depth" : 3.02 * mm, "hasSecondDirection" : true, "secondDirectionOppositeDirection" : false, "secondDirectionDepth" : 2.62 * mm});
        }
        {
            var Q0;
            Q0=makeQuery(id+"F7.opExtrude","CAP_EDGE",EDGE,{"disambiguationData":[OSD([sQuery(id+"F6.wireOp",EDGE,"E272.4")])],"isStart":true});
            var Q1;
            Q1=makeQuery(id+"F7.opExtrude","CAP_EDGE",EDGE,{"disambiguationData":[OSD([sQuery(id+"F6.wireOp",EDGE,"E272.3")])],"isStart":true});
            var Q2;
            Q2=makeQuery(id+"F7.opExtrude","CAP_EDGE",EDGE,{"disambiguationData":[OSD([sQuery(id+"F6.wireOp",EDGE,"E272.2")])],"isStart":true});
            fillet(context, id + "F8", {"entities" : qUnion([Q0, Q1, Q2]), "radius" : 3.05 * mm, "tangentPropagation" : true, "allowEdgeOverflow" : false});
        }
        {
            var Q0;
            Q0=makeQuery(id+"F7.opExtrude","CAP_EDGE",EDGE,{"disambiguationData":[OSD([sQuery(id+"F6.wireOp",EDGE,"E272.4")])],"isStart":false});
            fillet(context, id + "F9", {"entities" : qUnion([Q0]), "radius" : 0.56 * mm, "tangentPropagation" : true, "allowEdgeOverflow" : false});
        }
        {
            var Q0;
            Q0=makeQuery(id+"F1.opExtrude","SWEPT_BODY",BODY,{"disambiguationData":[OSD([sQuery(id+"F0.wireOp",EDGE,"E254"),sQuery(id+"F0.wireOp",EDGE,"E255"),sQuery(id+"F0.wireOp",EDGE,"E256"),sQuery(id+"F0.wireOp",EDGE,"E257"),sQuery(id+"F0.wireOp",EDGE,"E258"),sQuery(id+"F0.wireOp",EDGE,"E259"),sQuery(id+"F0.wireOp",EDGE,"E260"),sQuery(id+"F0.wireOp",EDGE,"E261"),sQuery(id+"F0.wireOp",EDGE,"E262"),sQuery(id+"F0.wireOp",EDGE,"E263"),sQuery(id+"F0.wireOp",EDGE,"E264"),sQuery(id+"F0.wireOp",EDGE,"E265"),sQuery(id+"F0.wireOp",EDGE,"E266"),sQuery(id+"F0.wireOp",EDGE,"E267"),sQuery(id+"F0.wireOp",EDGE,"E268"),sQuery(id+"F0.wireOp",EDGE,"E269")])]});
            var Q1;
            Q1=makeQuery(id+"F7.opExtrude","SWEPT_BODY",BODY,{"disambiguationData":[OSD([sQuery(id+"F6.wireOp",EDGE,"E272.0"),sQuery(id+"F6.wireOp",EDGE,"E272.1"),sQuery(id+"F6.wireOp",EDGE,"E272.2"),sQuery(id+"F6.wireOp",EDGE,"E272.3"),sQuery(id+"F6.wireOp",EDGE,"E272.4"),sQuery(id+"F6.wireOp",EDGE,"E272.5"),sQuery(id+"F6.wireOp",EDGE,"E272.6"),sQuery(id+"F6.wireOp",EDGE,"E272.7"),sQuery(id+"F6.wireOp",EDGE,"E272.8"),sQuery(id+"F6.wireOp",EDGE,"E272.9"),sQuery(id+"F6.wireOp",EDGE,"E272.10"),sQuery(id+"F6.wireOp",EDGE,"E272.11"),sQuery(id+"F6.wireOp",EDGE,"E273.0")])]});
            booleanBodies(context, id + "F10", {"operationType" : BooleanOperationType.SUBTRACTION, "tools" : qUnion([Q0]), "targets" : qUnion([Q1]), "offset" : true, "offsetAll" : true, "offsetDistance" : 0.1 * mm, "keepTools" : true});
        }
    });
